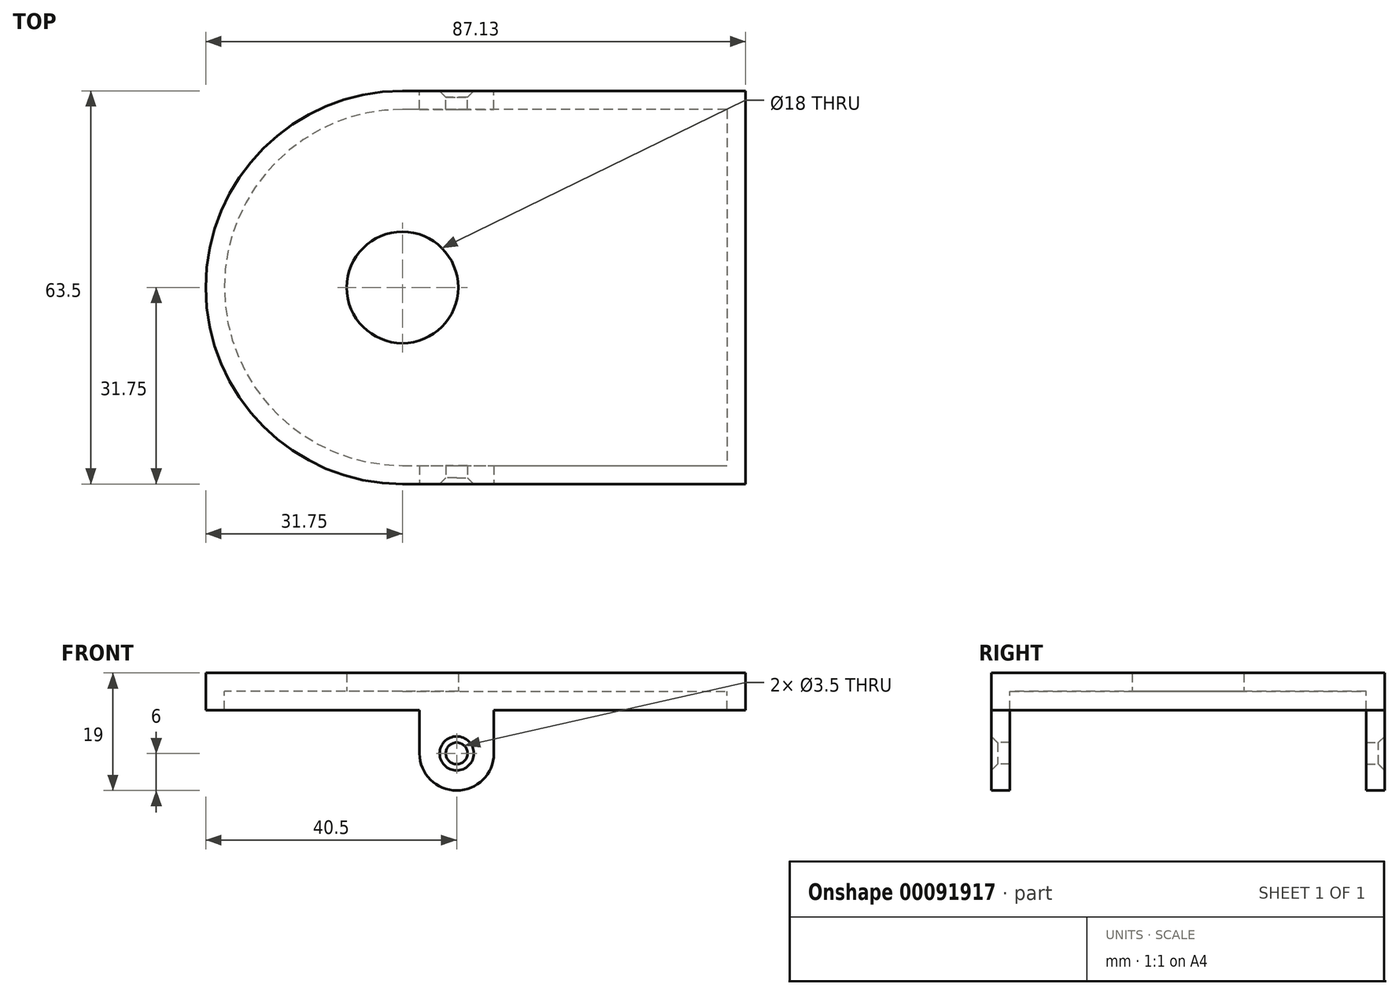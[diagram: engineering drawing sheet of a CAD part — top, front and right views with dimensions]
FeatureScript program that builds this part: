
annotation { "Feature Type Name" : "Feature", "Feature Type Description" : "" }
export const myFeature = defineFeature(function(context is Context, id is Id, definition is map)
    precondition{}
    {
        {
            var Q0;
            Q0=qCreatedBy(makeId("Top.planeOp"),FACE);
            var sketch = newSketch(context, id + "F0", { "sketchPlane" : qUnion([Q0])});
            skLineSegment(sketch, "E0.bottom", {"start": v(55.38, 31.75) * mm, "end": v(0, 31.75) * mm});
            skLineSegment(sketch, "E0.left", {"start": v(55.38, 31.75) * mm, "end": v(55.38, -31.75) * mm});
            skArc(sketch, "E1", {"start": v(0, 31.75) * mm, "mid": v(-31.75, 0) * mm, "end": v(0, -31.75) * mm});
            skCircle(sketch, "E2", {"center": v(0, 0) * mm, "radius": 9 * mm});
            skLineSegment(sketch, "E3", {"start": v(0, -31.75) * mm, "end": v(55.38, -31.75) * mm});
            skLineSegment(sketch, "E4.bottom", {"start": v(49.38, 16.25) * mm, "end": v(16.88, 16.25) * mm, "construction": true});
            skLineSegment(sketch, "E4.top", {"start": v(49.38, -16.25) * mm, "end": v(16.88, -16.25) * mm, "construction": true});
            skLineSegment(sketch, "E4.left", {"start": v(49.38, 16.25) * mm, "end": v(49.38, -16.25) * mm, "construction": true});
            skLineSegment(sketch, "E4.right", {"start": v(16.88, 16.25) * mm, "end": v(16.88, -16.25) * mm, "construction": true});
            skPoint(sketch, "E4.middle", {"position": v(33.12, 0) * mm});
            skCircle(sketch, "E5", {"center": v(0, 0) * mm, "radius": 28.75 * mm, "construction": true});
            skSolve(sketch);
        }
        {
            var Q0;
            {var subQ2=sQuery(id+"F0.wireOp",EDGE,"E0.bottom");Q0=makeQuery(id+"F0.imprint","IMPRINT",FACE,{"disambiguationData":[TD([[makeQuery(id+"F0.imprint","IMPRINT",EDGE,{"derivedFrom":subQ2}),1.0]])]});}
            var Q1;
            {var subQ3=sQuery(id+"F0.wireOp",EDGE,"Dg2Z6mpn-Rwp4-46km-Hi8r-SeTPOFQvzU17");Q1=makeQuery(id+"F0.imprint","IMPRINT",FACE,{"disambiguationData":[TD([[makeQuery(id+"F0.imprint","IMPRINT",EDGE,{"derivedFrom":subQ3}),1.0]])]});}
            var Q2;
            {var subQ0=sQuery(id+"F0.wireOp",EDGE,"E1");var subQ1=sQuery(id+"F0.wireOp",EDGE,"E0.right");var subQ2=makeQuery(id+"F0.imprint","INTERSECT",VERTEX,{"derivedFrom":[sQuery(id+"F0.wireOp",EDGE,"E0.bottom"),subQ1,subQ0]});Q2=makeQuery(id+"F0.imprint","IMPRINT",FACE,{"disambiguationData":[TD([[makeQuery(id+"F0.imprint","IMPRINT",EDGE,{"disambiguationData":[TD([[subQ2,-1.0]])],"derivedFrom":subQ1}),1.0]])]});}
            var Q3;
            {var subQ3=sQuery(id+"F0.wireOp",EDGE,"OEYcZ4KX-p0bM-T8b8-1sIX-PxLpcgBBKnbP");Q3=makeQuery(id+"F0.imprint","IMPRINT",FACE,{"disambiguationData":[TD([[makeQuery(id+"F0.imprint","IMPRINT",EDGE,{"derivedFrom":subQ3}),-1.0]])]});}
            extrude(context, id + "F1", {"entities" : qUnion([Q0, Q1, Q2, Q3]), "depth" : 3 * mm});
        }
        {
            var Q0;
            Q0=makeQuery(id+"F1.opExtrude","CAP_FACE",FACE,{"disambiguationData":[OSD([sQuery(id+"F0.wireOp",EDGE,"E0.bottom"),sQuery(id+"F0.wireOp",EDGE,"E0.left"),sQuery(id+"F0.wireOp",EDGE,"E1"),sQuery(id+"F0.wireOp",EDGE,"E2"),sQuery(id+"F0.wireOp",EDGE,"E3")])],"isStart":true});
            var sketch = newSketch(context, id + "F2", { "sketchPlane" : qUnion([Q0])});
            skArc(sketch, "E6.0", {"start": v(0, -28.75) * mm, "mid": v(-28.75, 0) * mm, "end": v(0, 28.75) * mm});
            skLineSegment(sketch, "E6.1", {"start": v(52.38, -28.75) * mm, "end": v(0, -28.75) * mm});
            skLineSegment(sketch, "E6.2", {"start": v(52.38, -28.75) * mm, "end": v(52.38, 28.75) * mm});
            skLineSegment(sketch, "E6.3", {"start": v(0, 28.75) * mm, "end": v(52.38, 28.75) * mm});
            skArc(sketch, "E7.0", {"start": v(0, -31.75) * mm, "mid": v(-31.75, 0) * mm, "end": v(0, 31.75) * mm});
            skLineSegment(sketch, "E7.1", {"start": v(0, 31.75) * mm, "end": v(55.38, 31.75) * mm});
            skLineSegment(sketch, "E7.2", {"start": v(55.38, -31.75) * mm, "end": v(55.38, 31.75) * mm});
            skLineSegment(sketch, "E7.3", {"start": v(55.38, -31.75) * mm, "end": v(0, -31.75) * mm});
            skSolve(sketch);
        }
        {
            var Q0;
            Q0 = qSketchRegion(id + "F2", true);
            extrude(context, id + "F3", {"entities" : qUnion([Q0]), "operationType" : NewBodyOperationType.ADD, "depth" : 3 * mm});
        }
        {
            var Q0;
            Q0=makeQuery(id+"F3.boolean.opBoolean","MERGE",FACE,{"derivedFrom":[makeQuery(id+"F1.opExtrude","SWEPT_FACE",FACE,{"disambiguationData":[OSD([sQuery(id+"F0.wireOp",EDGE,"E3")])]}),makeQuery(id+"F3.opExtrude","SWEPT_FACE",FACE,{"disambiguationData":[OSD([sQuery(id+"F2.wireOp",EDGE,"E7.1")])]})]});
            var sketch = newSketch(context, id + "F4", { "sketchPlane" : qUnion([Q0])});
            skLineSegment(sketch, "E8", {"start": v(8.75, 0) * mm, "end": v(8.75, -10) * mm, "construction": true});
            skCircle(sketch, "E9", {"center": v(8.75, -10) * mm, "radius": 1.75 * mm});
            skLineSegment(sketch, "E10", {"start": v(2.75, -3) * mm, "end": v(2.75, -10) * mm});
            skLineSegment(sketch, "E11.MirrorCS", {"start": v(14.75, -3) * mm, "end": v(14.75, -10) * mm});
            skArc(sketch, "E12", {"start": v(2.75, -10) * mm, "mid": v(8.75, -16) * mm, "end": v(14.75, -10) * mm});
            skSolve(sketch);
        }
        {
            var Q0;
            Q0=makeQuery(id+"F4.imprint","IMPRINT",FACE,{"disambiguationData":[TD([[makeQuery(id+"F4.imprint","IMPRINT",EDGE,{"derivedFrom":sQuery(id+"F4.wireOp",EDGE,"E9")}),-1.0]])]});
            extrude(context, id + "F5", {"entities" : qUnion([Q0]), "operationType" : NewBodyOperationType.ADD, "oppositeDirection" : true, "depth" : 3 * mm});
        }
        {
            var Q0;
            Q0=makeQuery(id+"F1.opExtrude","SWEPT_BODY",BODY,{"disambiguationData":[OSD([sQuery(id+"F0.wireOp",EDGE,"E0.bottom"),sQuery(id+"F0.wireOp",EDGE,"E0.left"),sQuery(id+"F0.wireOp",EDGE,"E1"),sQuery(id+"F0.wireOp",EDGE,"E2"),sQuery(id+"F0.wireOp",EDGE,"E3")])]});
            var Q1;
            Q1=qCreatedBy(makeId("Front.planeOp"),FACE);
            mirror(context, id + "F6", {"operationType" : NewBodyOperationType.ADD, "entities" : qUnion([Q0]), "mirrorPlane" : qUnion([Q1])});
        }
        {
            var Q0;
            Q0=makeQuery(id+"F5.opExtrude","CAP_EDGE",EDGE,{"disambiguationData":[OSD([sQuery(id+"F4.wireOp",EDGE,"E9")])],"isStart":true});
            var Q1;
            Q1=makeQuery(id+"F6.opPattern","COPY",EDGE,{"derivedFrom":makeQuery(id+"F5.opExtrude","CAP_EDGE",EDGE,{"disambiguationData":[OSD([sQuery(id+"F4.wireOp",EDGE,"E9")])],"isStart":true}),"instanceName":"1"});
            chamfer(context, id + "F7", {"entities" : qUnion([Q0, Q1]), "width" : 1 * mm, "tangentPropagation" : true});
        }
    });
